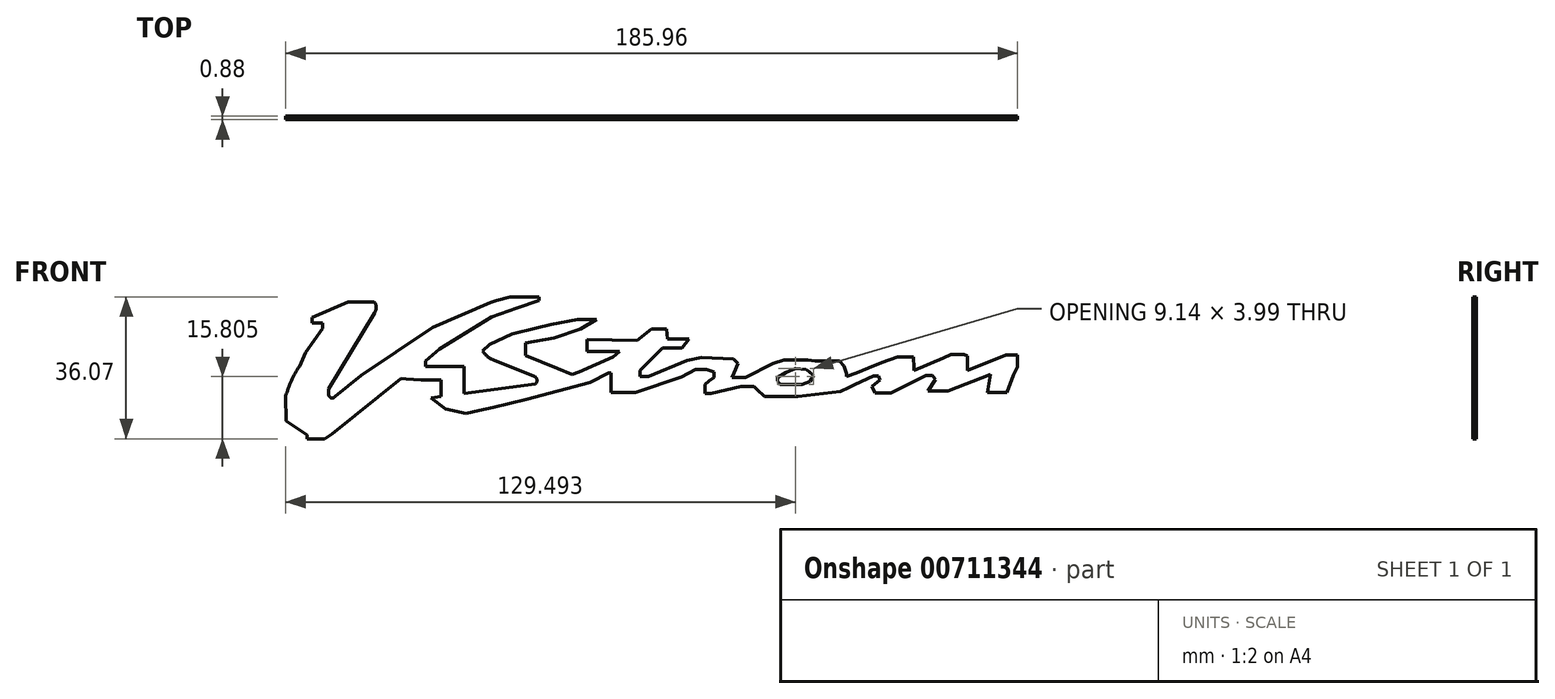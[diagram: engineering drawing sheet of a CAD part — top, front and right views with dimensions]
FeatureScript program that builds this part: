
annotation { "Feature Type Name" : "Feature", "Feature Type Description" : "" }
export const myFeature = defineFeature(function(context is Context, id is Id, definition is map)
    precondition{}
    {
        {
            var Q0;
            Q0=qCreatedBy(makeId("Front.planeOp"),FACE);
            var sketch = newSketch(context, id + "F0", { "sketchPlane" : qUnion([Q0])});
            skLineSegment(sketch, "E0", {"start": v(61.18, 22.23) * mm, "end": v(67.3, 23.37) * mm});
            skLineSegment(sketch, "E1", {"start": v(67.3, 23.37) * mm, "end": v(70.1, 23.37) * mm});
            skLineSegment(sketch, "E2", {"start": v(70.1, 23.37) * mm, "end": v(71.75, 23.37) * mm});
            skLineSegment(sketch, "E3", {"start": v(71.75, 23.37) * mm, "end": v(68, 21.28) * mm});
            skLineSegment(sketch, "E4", {"start": v(68, 21.28) * mm, "end": v(61.86, 19.14) * mm});
            skLineSegment(sketch, "E5", {"start": v(61.86, 19.14) * mm, "end": v(55.32, 17.94) * mm});
            skLineSegment(sketch, "E6", {"start": v(55.32, 17.94) * mm, "end": v(55.32, 15.1) * mm});
            skLineSegment(sketch, "E7", {"start": v(55.32, 15.1) * mm, "end": v(62.67, 12.12) * mm});
            skLineSegment(sketch, "E8", {"start": v(62.67, 12.12) * mm, "end": v(66, 10.76) * mm});
            skLineSegment(sketch, "E9", {"start": v(66, 10.76) * mm, "end": v(67.6, 11.32) * mm});
            skLineSegment(sketch, "E10", {"start": v(67.6, 11.32) * mm, "end": v(75.53, 14.78) * mm});
            skLineSegment(sketch, "E11", {"start": v(75.53, 14.78) * mm, "end": v(77.05, 16.07) * mm});
            skLineSegment(sketch, "E12", {"start": v(77.05, 16.07) * mm, "end": v(69.52, 16.07) * mm});
            skLineSegment(sketch, "E13", {"start": v(69.52, 16.07) * mm, "end": v(69.52, 18.83) * mm});
            skLineSegment(sketch, "E14", {"start": v(69.52, 18.83) * mm, "end": v(81.09, 18.6) * mm});
            skLineSegment(sketch, "E15", {"start": v(81.09, 18.6) * mm, "end": v(84.4, 21.29) * mm});
            skLineSegment(sketch, "E16", {"start": v(84.4, 21.29) * mm, "end": v(87.87, 21.29) * mm});
            skLineSegment(sketch, "E17", {"start": v(87.87, 21.29) * mm, "end": v(88.07, 18.87) * mm});
            skLineSegment(sketch, "E18", {"start": v(88.07, 18.87) * mm, "end": v(93.1, 18.87) * mm});
            skLineSegment(sketch, "E19", {"start": v(93.1, 18.87) * mm, "end": v(91.44, 16.8) * mm});
            skLineSegment(sketch, "E20", {"start": v(91.44, 16.8) * mm, "end": v(86.88, 16.8) * mm});
            skLineSegment(sketch, "E21", {"start": v(86.88, 16.8) * mm, "end": v(81.75, 11.67) * mm});
            skLineSegment(sketch, "E22", {"start": v(81.75, 11.67) * mm, "end": v(81.75, 10.24) * mm});
            skLineSegment(sketch, "E23", {"start": v(81.75, 10.24) * mm, "end": v(83.7, 10.24) * mm});
            skLineSegment(sketch, "E24", {"start": v(83.7, 10.24) * mm, "end": v(92.6, 13.94) * mm});
            skLineSegment(sketch, "E25", {"start": v(92.6, 13.94) * mm, "end": v(95.98, 14.63) * mm});
            skLineSegment(sketch, "E26", {"start": v(95.98, 14.63) * mm, "end": v(103.29, 14.27) * mm});
            skLineSegment(sketch, "E27", {"start": v(103.29, 14.27) * mm, "end": v(104.36, 13.3) * mm});
            skLineSegment(sketch, "E28", {"start": v(104.36, 13.3) * mm, "end": v(103.4, 11.1) * mm});
            skLineSegment(sketch, "E29", {"start": v(103.4, 11.1) * mm, "end": v(102.94, 10.06) * mm});
            skLineSegment(sketch, "E30", {"start": v(102.94, 10.06) * mm, "end": v(103.99, 10.06) * mm});
            skLineSegment(sketch, "E31", {"start": v(103.99, 10.06) * mm, "end": v(106.08, 10.06) * mm});
            skLineSegment(sketch, "E32", {"start": v(106.08, 10.06) * mm, "end": v(112.49, 13.2) * mm});
            skLineSegment(sketch, "E33", {"start": v(112.49, 13.2) * mm, "end": v(115.03, 14.1) * mm});
            skLineSegment(sketch, "E34", {"start": v(115.03, 14.1) * mm, "end": v(118.01, 14.1) * mm});
            skLineSegment(sketch, "E35", {"start": v(118.01, 14.1) * mm, "end": v(120.48, 14.1) * mm});
            skLineSegment(sketch, "E36", {"start": v(120.48, 14.1) * mm, "end": v(122.09, 13.88) * mm});
            skLineSegment(sketch, "E37", {"start": v(120.12, 11.9) * mm, "end": v(117.66, 12.07) * mm});
            skLineSegment(sketch, "E38", {"start": v(117.66, 12.07) * mm, "end": v(115.44, 11.18) * mm});
            skLineSegment(sketch, "E39", {"start": v(115.44, 11.18) * mm, "end": v(113.46, 10.06) * mm});
            skLineSegment(sketch, "E40", {"start": v(113.46, 10.06) * mm, "end": v(113.46, 9.22) * mm});
            skLineSegment(sketch, "E41", {"start": v(113.46, 9.22) * mm, "end": v(114.02, 8.44) * mm});
            skLineSegment(sketch, "E42", {"start": v(114.02, 8.44) * mm, "end": v(115.03, 8.44) * mm});
            skLineSegment(sketch, "E43", {"start": v(115.03, 8.44) * mm, "end": v(117.62, 8.44) * mm});
            skLineSegment(sketch, "E44", {"start": v(117.62, 8.44) * mm, "end": v(119.13, 8.44) * mm});
            skLineSegment(sketch, "E45", {"start": v(-35.24, 14.16) * mm, "end": v(-35.24, 14.16) * mm});
            skLineSegment(sketch, "E46", {"start": v(119.13, 8.44) * mm, "end": v(120.95, 9.06) * mm});
            skLineSegment(sketch, "E47", {"start": v(120.95, 9.06) * mm, "end": v(121.77, 10.51) * mm});
            skLineSegment(sketch, "E48", {"start": v(121.77, 10.51) * mm, "end": v(120.7, 11.4) * mm});
            skLineSegment(sketch, "E49", {"start": v(120.7, 11.4) * mm, "end": v(120.12, 11.9) * mm});
            skLineSegment(sketch, "E50", {"start": v(122.09, 13.88) * mm, "end": v(127.78, 13.88) * mm});
            skLineSegment(sketch, "E51", {"start": v(127.78, 13.88) * mm, "end": v(128.8, 12.7) * mm});
            skLineSegment(sketch, "E52", {"start": v(128.8, 12.7) * mm, "end": v(129.41, 10.9) * mm});
            skLineSegment(sketch, "E53", {"start": v(129.41, 10.9) * mm, "end": v(129.41, 10.23) * mm});
            skLineSegment(sketch, "E54", {"start": v(129.41, 10.23) * mm, "end": v(131.71, 11.13) * mm});
            skLineSegment(sketch, "E55", {"start": v(131.71, 11.13) * mm, "end": v(134.48, 12.2) * mm});
            skLineSegment(sketch, "E56", {"start": v(134.48, 12.2) * mm, "end": v(137.66, 13.45) * mm});
            skLineSegment(sketch, "E57", {"start": v(137.66, 13.45) * mm, "end": v(141.15, 14.8) * mm});
            skLineSegment(sketch, "E58", {"start": v(141.15, 14.8) * mm, "end": v(144.88, 14.8) * mm});
            skLineSegment(sketch, "E59", {"start": v(144.88, 14.8) * mm, "end": v(145, 12.25) * mm});
            skLineSegment(sketch, "E60", {"start": v(145, 12.25) * mm, "end": v(145.02, 11.64) * mm});
            skLineSegment(sketch, "E61", {"start": v(145.02, 11.64) * mm, "end": v(151.78, 14.55) * mm});
            skLineSegment(sketch, "E62", {"start": v(151.78, 14.55) * mm, "end": v(153.53, 15.3) * mm});
            skLineSegment(sketch, "E63", {"start": v(153.53, 15.3) * mm, "end": v(156.55, 15.3) * mm});
            skLineSegment(sketch, "E64", {"start": v(156.55, 15.3) * mm, "end": v(157.39, 14.97) * mm});
            skLineSegment(sketch, "E65", {"start": v(157.39, 14.97) * mm, "end": v(157.39, 12.95) * mm});
            skLineSegment(sketch, "E66", {"start": v(157.39, 12.95) * mm, "end": v(157.39, 12.28) * mm});
            skLineSegment(sketch, "E67", {"start": v(157.39, 12.28) * mm, "end": v(157.39, 11.6) * mm});
            skLineSegment(sketch, "E68", {"start": v(157.39, 11.6) * mm, "end": v(166.26, 15.27) * mm});
            skLineSegment(sketch, "E69", {"start": v(166.26, 15.27) * mm, "end": v(168.95, 15.27) * mm});
            skLineSegment(sketch, "E70", {"start": v(168.95, 15.27) * mm, "end": v(168.95, 12.49) * mm});
            skLineSegment(sketch, "E71", {"start": v(168.95, 12.49) * mm, "end": v(168.03, 10.64) * mm});
            skLineSegment(sketch, "E72", {"start": v(8.4, 22.6) * mm, "end": v(8.4, 21.37) * mm});
            skLineSegment(sketch, "E73", {"start": v(8.4, 21.37) * mm, "end": v(4.54, 15.76) * mm});
            skLineSegment(sketch, "E74", {"start": v(4.54, 15.76) * mm, "end": v(3.07, 12.62) * mm});
            skLineSegment(sketch, "E75", {"start": v(9.86, 7.43) * mm, "end": v(9.86, 5.91) * mm});
            skArc(sketch, "E76", {"start": v(9.86, 6.28) * mm, "mid": v(10.32, 5.35) * mm, "end": v(11.32, 5.64) * mm});
            skLineSegment(sketch, "E77", {"start": v(11.32, 5.64) * mm, "end": v(17.38, 10.52) * mm});
            skLineSegment(sketch, "E78", {"start": v(17.38, 10.52) * mm, "end": v(25.44, 15.92) * mm});
            skLineSegment(sketch, "E79", {"start": v(25.44, 15.92) * mm, "end": v(33.85, 21.57) * mm});
            skLineSegment(sketch, "E80", {"start": v(33.85, 21.57) * mm, "end": v(47.2, 27.4) * mm});
            skLineSegment(sketch, "E81", {"start": v(47.2, 27.4) * mm, "end": v(48.62, 27.8) * mm});
            skLineSegment(sketch, "E82", {"start": v(48.62, 27.8) * mm, "end": v(51.72, 28.68) * mm});
            skLineSegment(sketch, "E83", {"start": v(51.72, 28.68) * mm, "end": v(58.4, 28.68) * mm});
            skLineSegment(sketch, "E84", {"start": v(58.4, 28.68) * mm, "end": v(58.4, 27.8) * mm});
            skLineSegment(sketch, "E85", {"start": v(58.4, 27.8) * mm, "end": v(53.3, 26.05) * mm});
            skLineSegment(sketch, "E86", {"start": v(53.3, 26.05) * mm, "end": v(47.42, 24.02) * mm});
            skLineSegment(sketch, "E87", {"start": v(47.42, 24.02) * mm, "end": v(35.42, 16.61) * mm});
            skLineSegment(sketch, "E88", {"start": v(35.42, 16.61) * mm, "end": v(32.2, 13.86) * mm});
            skLineSegment(sketch, "E89", {"start": v(32.2, 13.86) * mm, "end": v(32.2, 12.57) * mm});
            skLineSegment(sketch, "E90", {"start": v(32.2, 12.57) * mm, "end": v(41.05, 12.57) * mm});
            skLineSegment(sketch, "E91", {"start": v(33.43, 5.28) * mm, "end": v(35.83, 5.6) * mm});
            skLineSegment(sketch, "E92", {"start": v(4.85, -4.12) * mm, "end": v(8.9, -4.11) * mm});
            skLineSegment(sketch, "E93", {"start": v(0, 0) * mm, "end": v(4.85, -3.21) * mm});
            skLineSegment(sketch, "E94", {"start": v(4.85, -3.21) * mm, "end": v(4.85, -4.12) * mm});
            skLineSegment(sketch, "E95", {"start": v(5.96, 22.6) * mm, "end": v(5.96, 23.91) * mm});
            skLineSegment(sketch, "E96", {"start": v(5.96, 23.91) * mm, "end": v(14.33, 27.5) * mm});
            skLineSegment(sketch, "E97", {"start": v(14.33, 27.5) * mm, "end": v(20.37, 27.5) * mm});
            skLineSegment(sketch, "E98", {"start": v(20.4, 24.92) * mm, "end": v(9.86, 7.43) * mm});
            skLineSegment(sketch, "E99", {"start": v(5.96, 22.6) * mm, "end": v(8.4, 22.6) * mm});
            skArc(sketch, "E100", {"start": v(20.4, 24.92) * mm, "mid": v(20.82, 26.21) * mm, "end": v(20.37, 27.5) * mm});
            skLineSegment(sketch, "E101", {"start": v(57.34, 10.31) * mm, "end": v(47.91, 14.1) * mm});
            skLineSegment(sketch, "E102", {"start": v(45.36, 16.2) * mm, "end": v(47, 17.65) * mm});
            skLineSegment(sketch, "E103", {"start": v(47, 17.65) * mm, "end": v(52.22, 20.04) * mm});
            skLineSegment(sketch, "E104", {"start": v(52.22, 20.04) * mm, "end": v(57.84, 21.41) * mm});
            skLineSegment(sketch, "E105", {"start": v(57.84, 21.41) * mm, "end": v(61.18, 22.23) * mm});
            skArc(sketch, "E106", {"start": v(45.36, 16.2) * mm, "mid": v(46.45, 14.92) * mm, "end": v(47.91, 14.1) * mm});
            skArc(sketch, "E107", {"start": v(57.64, 8.58) * mm, "mid": v(57.89, 9.64) * mm, "end": v(57.12, 10.4) * mm});
            skLineSegment(sketch, "E108", {"start": v(166.46, 6.55) * mm, "end": v(161.99, 6.55) * mm});
            skLineSegment(sketch, "E109", {"start": v(161.99, 6.55) * mm, "end": v(162.63, 10.72) * mm});
            skLineSegment(sketch, "E110", {"start": v(162.63, 10.72) * mm, "end": v(152.81, 6.9) * mm});
            skLineSegment(sketch, "E111", {"start": v(152.81, 6.9) * mm, "end": v(148.28, 6.9) * mm});
            skLineSegment(sketch, "E112", {"start": v(148.28, 6.9) * mm, "end": v(149.93, 9.6) * mm});
            skLineSegment(sketch, "E113", {"start": v(149.93, 9.6) * mm, "end": v(149.22, 10.48) * mm});
            skLineSegment(sketch, "E114", {"start": v(149.22, 10.48) * mm, "end": v(147.75, 10.48) * mm});
            skLineSegment(sketch, "E115", {"start": v(147.75, 10.48) * mm, "end": v(139.7, 6.43) * mm});
            skLineSegment(sketch, "E116", {"start": v(139.7, 6.43) * mm, "end": v(136.05, 6.43) * mm});
            skLineSegment(sketch, "E117", {"start": v(136.05, 6.43) * mm, "end": v(135.34, 7.9) * mm});
            skLineSegment(sketch, "E118", {"start": v(135.34, 7.9) * mm, "end": v(137.1, 9.49) * mm});
            skLineSegment(sketch, "E119", {"start": v(137.1, 9.49) * mm, "end": v(136.82, 10.43) * mm});
            skLineSegment(sketch, "E120", {"start": v(136.82, 10.43) * mm, "end": v(135.61, 10.43) * mm});
            skLineSegment(sketch, "E121", {"start": v(135.61, 10.43) * mm, "end": v(131.41, 8.4) * mm});
            skLineSegment(sketch, "E122", {"start": v(131.41, 8.4) * mm, "end": v(129.95, 7.68) * mm});
            skLineSegment(sketch, "E123", {"start": v(129.95, 7.68) * mm, "end": v(128.02, 6.75) * mm});
            skLineSegment(sketch, "E124", {"start": v(128.02, 6.75) * mm, "end": v(121.39, 6) * mm});
            skLineSegment(sketch, "E125", {"start": v(121.39, 6) * mm, "end": v(118.26, 5.64) * mm});
            skLineSegment(sketch, "E126", {"start": v(118.26, 5.64) * mm, "end": v(112.75, 5.64) * mm});
            skLineSegment(sketch, "E127", {"start": v(112.75, 5.64) * mm, "end": v(110.45, 5.64) * mm});
            skLineSegment(sketch, "E128", {"start": v(110.45, 5.64) * mm, "end": v(108.8, 7.27) * mm});
            skLineSegment(sketch, "E129", {"start": v(108.8, 7.27) * mm, "end": v(108.1, 7.96) * mm});
            skLineSegment(sketch, "E130", {"start": v(108.1, 7.96) * mm, "end": v(107.3, 7.96) * mm});
            skLineSegment(sketch, "E131", {"start": v(107.3, 7.96) * mm, "end": v(105.01, 7.96) * mm});
            skLineSegment(sketch, "E132", {"start": v(105.01, 7.96) * mm, "end": v(98.13, 6.37) * mm});
            skLineSegment(sketch, "E133", {"start": v(98.13, 6.37) * mm, "end": v(96.74, 6.37) * mm});
            skLineSegment(sketch, "E134", {"start": v(96.74, 6.37) * mm, "end": v(96.74, 8.45) * mm});
            skLineSegment(sketch, "E135", {"start": v(96.74, 8.45) * mm, "end": v(97.7, 9.2) * mm});
            skLineSegment(sketch, "E136", {"start": v(97.7, 9.2) * mm, "end": v(98.82, 10.04) * mm});
            skLineSegment(sketch, "E137", {"start": v(98.82, 10.04) * mm, "end": v(98.77, 11.27) * mm});
            skLineSegment(sketch, "E138", {"start": v(98.77, 11.27) * mm, "end": v(97.06, 11.86) * mm});
            skLineSegment(sketch, "E139", {"start": v(97.06, 11.86) * mm, "end": v(94.56, 11.86) * mm});
            skLineSegment(sketch, "E140", {"start": v(94.56, 11.86) * mm, "end": v(91.36, 10.1) * mm});
            skLineSegment(sketch, "E141", {"start": v(91.36, 10.1) * mm, "end": v(80.65, 6.52) * mm});
            skLineSegment(sketch, "E142", {"start": v(80.65, 6.52) * mm, "end": v(77.45, 6.52) * mm});
            skLineSegment(sketch, "E143", {"start": v(77.45, 6.52) * mm, "end": v(75.05, 6.52) * mm});
            skLineSegment(sketch, "E144", {"start": v(75.05, 6.52) * mm, "end": v(75.05, 11.05) * mm});
            skLineSegment(sketch, "E145", {"start": v(75.05, 11.05) * mm, "end": v(74.4, 11.05) * mm});
            skLineSegment(sketch, "E146", {"start": v(74.4, 11.05) * mm, "end": v(70.14, 8.92) * mm});
            skLineSegment(sketch, "E147", {"start": v(70.14, 8.92) * mm, "end": v(55.44, 4.9) * mm});
            skLineSegment(sketch, "E148", {"start": v(55.44, 4.9) * mm, "end": v(47.76, 3.13) * mm});
            skLineSegment(sketch, "E149", {"start": v(47.76, 3.13) * mm, "end": v(44.61, 2.4) * mm});
            skLineSegment(sketch, "E150", {"start": v(44.61, 2.4) * mm, "end": v(41.52, 1.69) * mm});
            skLineSegment(sketch, "E151", {"start": v(41.52, 1.69) * mm, "end": v(36.86, 2.77) * mm});
            skLineSegment(sketch, "E152", {"start": v(36.86, 2.77) * mm, "end": v(33.43, 5.28) * mm});
            skLineSegment(sketch, "E153", {"start": v(-0.1, 5.7) * mm, "end": v(0, 0) * mm});
            skLineSegment(sketch, "E154", {"start": v(35.83, 9.43) * mm, "end": v(35.83, 5.6) * mm});
            skLineSegment(sketch, "E155", {"start": v(41.05, 12.57) * mm, "end": v(41.05, 6.32) * mm});
            skLineSegment(sketch, "E156", {"start": v(35.83, 9.43) * mm, "end": v(31.14, 9.43) * mm});
            skLineSegment(sketch, "E157", {"start": v(31.14, 9.43) * mm, "end": v(27.66, 9.7) * mm});
            skLineSegment(sketch, "E158", {"start": v(27.66, 9.7) * mm, "end": v(26.6, 9.77) * mm});
            skLineSegment(sketch, "E159", {"start": v(26.6, 9.77) * mm, "end": v(10.57, -2.96) * mm});
            skLineSegment(sketch, "E160", {"start": v(10.57, -2.96) * mm, "end": v(8.9, -4.11) * mm});
            skLineSegment(sketch, "E161", {"start": v(41.05, 6.32) * mm, "end": v(57.64, 8.58) * mm});
            skLineSegment(sketch, "E162", {"start": v(168.03, 10.64) * mm, "end": v(166.46, 6.55) * mm});
            skArc(sketch, "E163", {"start": v(3.07, 12.62) * mm, "mid": v(1.23, 9.28) * mm, "end": v(-0.1, 5.7) * mm});
            skSolve(sketch);
        }
        {
            var Q0;
            Q0=qSketchRegion(id+"F0",true);
            extrude(context, id + "F1", {"entities" : qUnion([Q0]), "depth" : .8 * mm, "offsetDistance" : 25 * mm});
        }
        {
            var Q0;
            Q0=makeQuery(id+"F1.opExtrude","SWEPT_BODY",BODY,{"disambiguationData":[OSD([sQuery(id+"F0.wireOp",EDGE,"E0"),sQuery(id+"F0.wireOp",EDGE,"E1"),sQuery(id+"F0.wireOp",EDGE,"E2"),sQuery(id+"F0.wireOp",EDGE,"E3"),sQuery(id+"F0.wireOp",EDGE,"E4"),sQuery(id+"F0.wireOp",EDGE,"E5"),sQuery(id+"F0.wireOp",EDGE,"E6"),sQuery(id+"F0.wireOp",EDGE,"E7"),sQuery(id+"F0.wireOp",EDGE,"E8"),sQuery(id+"F0.wireOp",EDGE,"E9"),sQuery(id+"F0.wireOp",EDGE,"E10"),sQuery(id+"F0.wireOp",EDGE,"E11"),sQuery(id+"F0.wireOp",EDGE,"E12"),sQuery(id+"F0.wireOp",EDGE,"E13"),sQuery(id+"F0.wireOp",EDGE,"E14"),sQuery(id+"F0.wireOp",EDGE,"E15"),sQuery(id+"F0.wireOp",EDGE,"E16"),sQuery(id+"F0.wireOp",EDGE,"E17"),sQuery(id+"F0.wireOp",EDGE,"E18"),sQuery(id+"F0.wireOp",EDGE,"E19"),sQuery(id+"F0.wireOp",EDGE,"E20"),sQuery(id+"F0.wireOp",EDGE,"E21"),sQuery(id+"F0.wireOp",EDGE,"E22"),sQuery(id+"F0.wireOp",EDGE,"E23"),sQuery(id+"F0.wireOp",EDGE,"E24"),sQuery(id+"F0.wireOp",EDGE,"E25"),sQuery(id+"F0.wireOp",EDGE,"E26"),sQuery(id+"F0.wireOp",EDGE,"E27"),sQuery(id+"F0.wireOp",EDGE,"E28"),sQuery(id+"F0.wireOp",EDGE,"E29"),sQuery(id+"F0.wireOp",EDGE,"E30"),sQuery(id+"F0.wireOp",EDGE,"E31"),sQuery(id+"F0.wireOp",EDGE,"E32"),sQuery(id+"F0.wireOp",EDGE,"E33"),sQuery(id+"F0.wireOp",EDGE,"E34"),sQuery(id+"F0.wireOp",EDGE,"E35"),sQuery(id+"F0.wireOp",EDGE,"E36"),sQuery(id+"F0.wireOp",EDGE,"E37"),sQuery(id+"F0.wireOp",EDGE,"E38"),sQuery(id+"F0.wireOp",EDGE,"E39"),sQuery(id+"F0.wireOp",EDGE,"E40"),sQuery(id+"F0.wireOp",EDGE,"E41"),sQuery(id+"F0.wireOp",EDGE,"E42"),sQuery(id+"F0.wireOp",EDGE,"E43"),sQuery(id+"F0.wireOp",EDGE,"E44"),sQuery(id+"F0.wireOp",EDGE,"E46"),sQuery(id+"F0.wireOp",EDGE,"E47"),sQuery(id+"F0.wireOp",EDGE,"E48"),sQuery(id+"F0.wireOp",EDGE,"E49"),sQuery(id+"F0.wireOp",EDGE,"E50"),sQuery(id+"F0.wireOp",EDGE,"E51"),sQuery(id+"F0.wireOp",EDGE,"E52"),sQuery(id+"F0.wireOp",EDGE,"E53"),sQuery(id+"F0.wireOp",EDGE,"E54"),sQuery(id+"F0.wireOp",EDGE,"E55"),sQuery(id+"F0.wireOp",EDGE,"E56"),sQuery(id+"F0.wireOp",EDGE,"E57"),sQuery(id+"F0.wireOp",EDGE,"E58"),sQuery(id+"F0.wireOp",EDGE,"E59"),sQuery(id+"F0.wireOp",EDGE,"E60"),sQuery(id+"F0.wireOp",EDGE,"E61"),sQuery(id+"F0.wireOp",EDGE,"E62"),sQuery(id+"F0.wireOp",EDGE,"E63"),sQuery(id+"F0.wireOp",EDGE,"E64"),sQuery(id+"F0.wireOp",EDGE,"E65"),sQuery(id+"F0.wireOp",EDGE,"E66"),sQuery(id+"F0.wireOp",EDGE,"E67"),sQuery(id+"F0.wireOp",EDGE,"E68"),sQuery(id+"F0.wireOp",EDGE,"E69"),sQuery(id+"F0.wireOp",EDGE,"E70"),sQuery(id+"F0.wireOp",EDGE,"E71"),sQuery(id+"F0.wireOp",EDGE,"E72"),sQuery(id+"F0.wireOp",EDGE,"E73"),sQuery(id+"F0.wireOp",EDGE,"E74"),sQuery(id+"F0.wireOp",EDGE,"E75"),sQuery(id+"F0.wireOp",EDGE,"E76"),sQuery(id+"F0.wireOp",EDGE,"E77"),sQuery(id+"F0.wireOp",EDGE,"E78"),sQuery(id+"F0.wireOp",EDGE,"E79"),sQuery(id+"F0.wireOp",EDGE,"E80"),sQuery(id+"F0.wireOp",EDGE,"E81"),sQuery(id+"F0.wireOp",EDGE,"E82"),sQuery(id+"F0.wireOp",EDGE,"E83"),sQuery(id+"F0.wireOp",EDGE,"E84"),sQuery(id+"F0.wireOp",EDGE,"E85"),sQuery(id+"F0.wireOp",EDGE,"E86"),sQuery(id+"F0.wireOp",EDGE,"E87"),sQuery(id+"F0.wireOp",EDGE,"E88"),sQuery(id+"F0.wireOp",EDGE,"E89"),sQuery(id+"F0.wireOp",EDGE,"E90"),sQuery(id+"F0.wireOp",EDGE,"E91"),sQuery(id+"F0.wireOp",EDGE,"E92"),sQuery(id+"F0.wireOp",EDGE,"E93"),sQuery(id+"F0.wireOp",EDGE,"E94"),sQuery(id+"F0.wireOp",EDGE,"E95"),sQuery(id+"F0.wireOp",EDGE,"E96"),sQuery(id+"F0.wireOp",EDGE,"E97"),sQuery(id+"F0.wireOp",EDGE,"E98"),sQuery(id+"F0.wireOp",EDGE,"E99"),sQuery(id+"F0.wireOp",EDGE,"E100"),sQuery(id+"F0.wireOp",EDGE,"E101"),sQuery(id+"F0.wireOp",EDGE,"E102"),sQuery(id+"F0.wireOp",EDGE,"E103"),sQuery(id+"F0.wireOp",EDGE,"E104"),sQuery(id+"F0.wireOp",EDGE,"E105"),sQuery(id+"F0.wireOp",EDGE,"E106"),sQuery(id+"F0.wireOp",EDGE,"E107"),sQuery(id+"F0.wireOp",EDGE,"E108"),sQuery(id+"F0.wireOp",EDGE,"E109"),sQuery(id+"F0.wireOp",EDGE,"E110"),sQuery(id+"F0.wireOp",EDGE,"E111"),sQuery(id+"F0.wireOp",EDGE,"E112"),sQuery(id+"F0.wireOp",EDGE,"E113"),sQuery(id+"F0.wireOp",EDGE,"E114"),sQuery(id+"F0.wireOp",EDGE,"E115"),sQuery(id+"F0.wireOp",EDGE,"E116"),sQuery(id+"F0.wireOp",EDGE,"E117"),sQuery(id+"F0.wireOp",EDGE,"E118"),sQuery(id+"F0.wireOp",EDGE,"E119"),sQuery(id+"F0.wireOp",EDGE,"E120"),sQuery(id+"F0.wireOp",EDGE,"E121"),sQuery(id+"F0.wireOp",EDGE,"E122"),sQuery(id+"F0.wireOp",EDGE,"E123"),sQuery(id+"F0.wireOp",EDGE,"E124"),sQuery(id+"F0.wireOp",EDGE,"E125"),sQuery(id+"F0.wireOp",EDGE,"E126"),sQuery(id+"F0.wireOp",EDGE,"E127"),sQuery(id+"F0.wireOp",EDGE,"E128"),sQuery(id+"F0.wireOp",EDGE,"E129"),sQuery(id+"F0.wireOp",EDGE,"E130"),sQuery(id+"F0.wireOp",EDGE,"E131"),sQuery(id+"F0.wireOp",EDGE,"E132"),sQuery(id+"F0.wireOp",EDGE,"E133"),sQuery(id+"F0.wireOp",EDGE,"E134"),sQuery(id+"F0.wireOp",EDGE,"E135"),sQuery(id+"F0.wireOp",EDGE,"E136"),sQuery(id+"F0.wireOp",EDGE,"E137"),sQuery(id+"F0.wireOp",EDGE,"E138"),sQuery(id+"F0.wireOp",EDGE,"E139"),sQuery(id+"F0.wireOp",EDGE,"E140"),sQuery(id+"F0.wireOp",EDGE,"E141"),sQuery(id+"F0.wireOp",EDGE,"E142"),sQuery(id+"F0.wireOp",EDGE,"E143"),sQuery(id+"F0.wireOp",EDGE,"E144"),sQuery(id+"F0.wireOp",EDGE,"E145"),sQuery(id+"F0.wireOp",EDGE,"E146"),sQuery(id+"F0.wireOp",EDGE,"E147"),sQuery(id+"F0.wireOp",EDGE,"E148"),sQuery(id+"F0.wireOp",EDGE,"E149"),sQuery(id+"F0.wireOp",EDGE,"E150"),sQuery(id+"F0.wireOp",EDGE,"E151"),sQuery(id+"F0.wireOp",EDGE,"E152"),sQuery(id+"F0.wireOp",EDGE,"E153"),sQuery(id+"F0.wireOp",EDGE,"E154"),sQuery(id+"F0.wireOp",EDGE,"E155"),sQuery(id+"F0.wireOp",EDGE,"E156"),sQuery(id+"F0.wireOp",EDGE,"E157"),sQuery(id+"F0.wireOp",EDGE,"E158"),sQuery(id+"F0.wireOp",EDGE,"E159"),sQuery(id+"F0.wireOp",EDGE,"E160"),sQuery(id+"F0.wireOp",EDGE,"E161"),sQuery(id+"F0.wireOp",EDGE,"E162"),sQuery(id+"F0.wireOp",EDGE,"E163")])]});
            var Q1;
            Q1=makeQuery(id+"F1.opExtrude","CAP_VERTEX",VERTEX,{"disambiguationData":[OSD([sQuery(id+"F0.wireOp",EDGE,"E95"),sQuery(id+"F0.wireOp",EDGE,"E96")])],"isStart":false});
            transform(context, id + "F2", {"entities" : qUnion([Q0]), "transformType" : TransformType.SCALE_UNIFORMLY, "scale" : 1.1, "scalePoint" : qUnion([Q1]), "makeCopy" : false});
        }
    });
